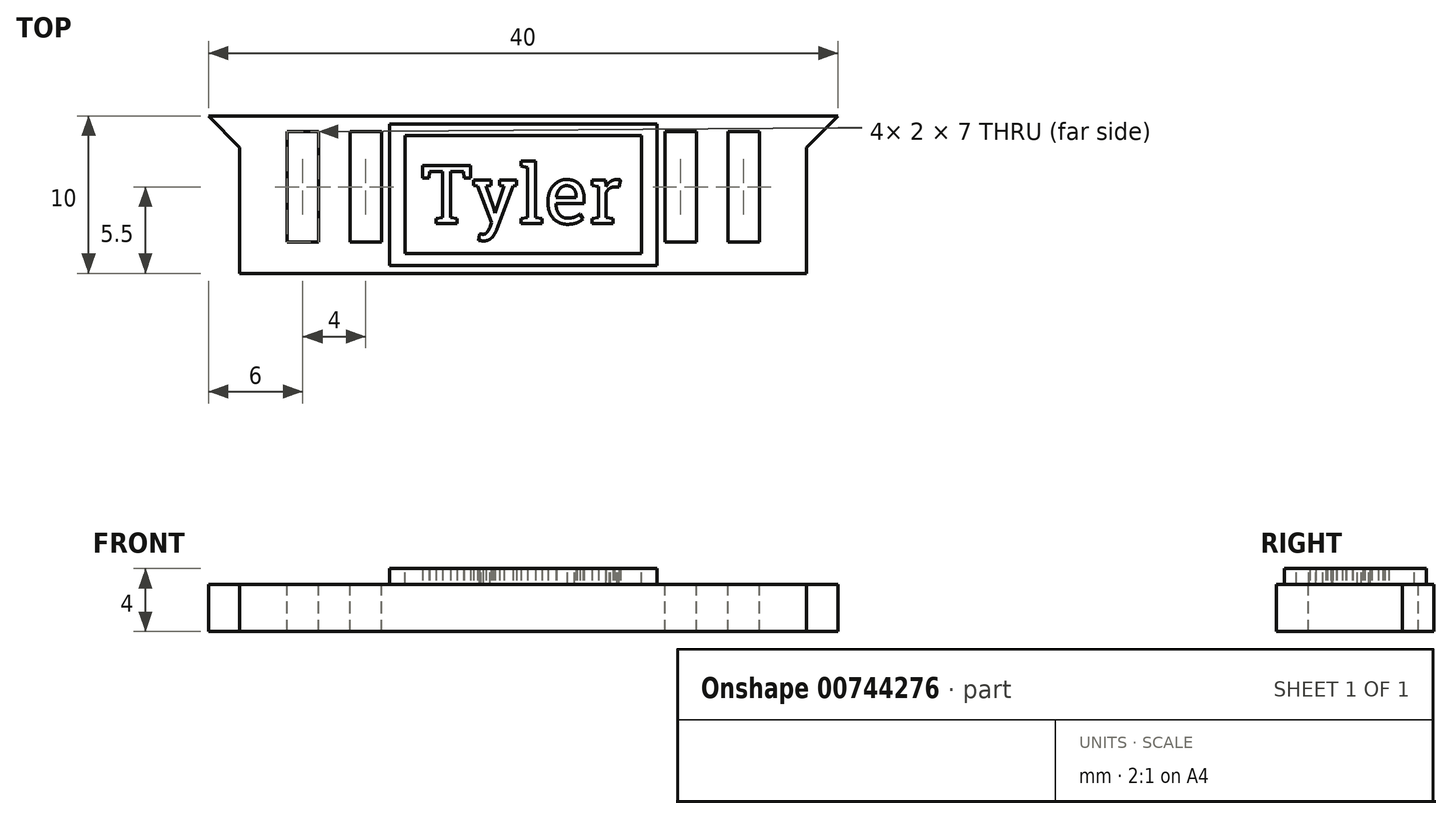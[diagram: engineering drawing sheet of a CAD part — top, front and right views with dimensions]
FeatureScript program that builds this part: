
annotation { "Feature Type Name" : "Feature", "Feature Type Description" : "" }
export const myFeature = defineFeature(function(context is Context, id is Id, definition is map)
    precondition{}
    {
        {
            var Q0;
            Q0=qCreatedBy(makeId("Top.planeOp"),FACE);
            var sketch = newSketch(context, id + "F0", { "sketchPlane" : qUnion([Q0])});
            skLineSegment(sketch, "E0.bottom", {"start": v(-18, 5) * mm, "end": v(18, 5) * mm});
            skLineSegment(sketch, "E0.top", {"start": v(-18, -5) * mm, "end": v(18, -5) * mm});
            skLineSegment(sketch, "E0.left", {"start": v(-18, 3) * mm, "end": v(-18, -5) * mm});
            skLineSegment(sketch, "E0.right", {"start": v(18, 3) * mm, "end": v(18, -5) * mm});
            skPoint(sketch, "E0.middle", {"position": v(0, 0) * mm});
            skLineSegment(sketch, "E1", {"start": v(18, 5) * mm, "end": v(20, 5) * mm});
            skLineSegment(sketch, "E2", {"start": v(20, 5) * mm, "end": v(18, 3) * mm});
            skLineSegment(sketch, "E3.MirrorCS", {"start": v(-20, 5) * mm, "end": v(-18, 3) * mm});
            skLineSegment(sketch, "E4.MirrorCS", {"start": v(-18, 5) * mm, "end": v(-20, 5) * mm});
            skSolve(sketch);
        }
        {
            var Q0;
            Q0=makeQuery(id+"F0.imprint","IMPRINT",FACE,{"disambiguationData":[TD([[makeQuery(id+"F0.imprint","IMPRINT",EDGE,{"derivedFrom":sQuery(id+"F0.wireOp",EDGE,"E0.bottom")}),-1.0]])]});
            extrude(context, id + "F1", {"entities" : qUnion([Q0]), "depth" : 3 * mm, "offsetDistance" : 25 * mm});
        }
        {
            var Q0;
            Q0=makeQuery(id+"F1.opExtrude","CAP_FACE",FACE,{"disambiguationData":[OSD([sQuery(id+"F0.wireOp",EDGE,"E0.bottom"),sQuery(id+"F0.wireOp",EDGE,"E0.top"),sQuery(id+"F0.wireOp",EDGE,"E0.left"),sQuery(id+"F0.wireOp",EDGE,"E0.right"),sQuery(id+"F0.wireOp",EDGE,"E1"),sQuery(id+"F0.wireOp",EDGE,"E2"),sQuery(id+"F0.wireOp",EDGE,"E3.MirrorCS"),sQuery(id+"F0.wireOp",EDGE,"E4.MirrorCS")])],"isStart":false});
            var sketch = newSketch(context, id + "F2", { "sketchPlane" : qUnion([Q0])});
            skLineSegment(sketch, "E5.bottom", {"start": v(-13, 4) * mm, "end": v(-15, 4) * mm});
            skLineSegment(sketch, "E5.top", {"start": v(-13, -3) * mm, "end": v(-15, -3) * mm});
            skLineSegment(sketch, "E5.left", {"start": v(-13, 4) * mm, "end": v(-13, -3) * mm});
            skLineSegment(sketch, "E5.right", {"start": v(-15, 4) * mm, "end": v(-15, -3) * mm});
            skLineSegment(sketch, "E6.1.0.0", {"start": v(-9, 4) * mm, "end": v(-9, -3) * mm});
            skLineSegment(sketch, "E6.1.0.1", {"start": v(-9, 4) * mm, "end": v(-11, 4) * mm});
            skLineSegment(sketch, "E6.1.0.2", {"start": v(-11, 4) * mm, "end": v(-11, -3) * mm});
            skLineSegment(sketch, "E6.1.0.3", {"start": v(-9, -3) * mm, "end": v(-11, -3) * mm});
            skLineSegment(sketch, "E6.2.0.0", {"start": v(-5, 4) * mm, "end": v(-5, -3) * mm});
            skLineSegment(sketch, "E6.2.0.1", {"start": v(-5, 4) * mm, "end": v(-7, 4) * mm});
            skLineSegment(sketch, "E6.2.0.2", {"start": v(-7, 4) * mm, "end": v(-7, -3) * mm});
            skLineSegment(sketch, "E6.2.0.3", {"start": v(-5, -3) * mm, "end": v(-7, -3) * mm});
            skLineSegment(sketch, "E6.3.0.0", {"start": v(-1, 4) * mm, "end": v(-1, -3) * mm});
            skLineSegment(sketch, "E6.3.0.1", {"start": v(-1, 4) * mm, "end": v(-3, 4) * mm});
            skLineSegment(sketch, "E6.3.0.2", {"start": v(-3, 4) * mm, "end": v(-3, -3) * mm});
            skLineSegment(sketch, "E6.3.0.3", {"start": v(-1, -3) * mm, "end": v(-3, -3) * mm});
            skLineSegment(sketch, "E6.4.0.0", {"start": v(3, 4) * mm, "end": v(3, -3) * mm});
            skLineSegment(sketch, "E6.4.0.1", {"start": v(3, 4) * mm, "end": v(1, 4) * mm});
            skLineSegment(sketch, "E6.4.0.2", {"start": v(1, 4) * mm, "end": v(1, -3) * mm});
            skLineSegment(sketch, "E6.4.0.3", {"start": v(3, -3) * mm, "end": v(1, -3) * mm});
            skLineSegment(sketch, "E6.5.0.0", {"start": v(7, 4) * mm, "end": v(7, -3) * mm});
            skLineSegment(sketch, "E6.5.0.1", {"start": v(7, 4) * mm, "end": v(5, 4) * mm});
            skLineSegment(sketch, "E6.5.0.2", {"start": v(5, 4) * mm, "end": v(5, -3) * mm});
            skLineSegment(sketch, "E6.5.0.3", {"start": v(7, -3) * mm, "end": v(5, -3) * mm});
            skLineSegment(sketch, "E6.6.0.0", {"start": v(11, 4) * mm, "end": v(11, -3) * mm});
            skLineSegment(sketch, "E6.6.0.1", {"start": v(11, 4) * mm, "end": v(9, 4) * mm});
            skLineSegment(sketch, "E6.6.0.2", {"start": v(9, 4) * mm, "end": v(9, -3) * mm});
            skLineSegment(sketch, "E6.6.0.3", {"start": v(11, -3) * mm, "end": v(9, -3) * mm});
            skLineSegment(sketch, "E6.7.0.0", {"start": v(15, 4) * mm, "end": v(15, -3) * mm});
            skLineSegment(sketch, "E6.7.0.1", {"start": v(15, 4) * mm, "end": v(13, 4) * mm});
            skLineSegment(sketch, "E6.7.0.2", {"start": v(13, 4) * mm, "end": v(13, -3) * mm});
            skLineSegment(sketch, "E6.7.0.3", {"start": v(15, -3) * mm, "end": v(13, -3) * mm});
            skLineSegment(sketch, "E6.direction1", {"start": v(-13, -3) * mm, "end": v(-9, -3) * mm, "construction": true});
            skSolve(sketch);
        }
        {
            var Q0;
            Q0 = qSketchRegion(id + "F2", true);
            extrude(context, id + "F3", {"entities" : qUnion([Q0]), "operationType" : NewBodyOperationType.REMOVE, "oppositeDirection" : true, "depth" : 25 * mm, "offsetDistance" : 25 * mm});
        }
        {
            var Q0;
            Q0=qCreatedBy(makeId("Top.planeOp"),FACE);
            var sketch = newSketch(context, id + "F4", { "sketchPlane" : qUnion([Q0])});
            skLineSegment(sketch, "E7.bottom", {"start": v(-8.5, 4.5) * mm, "end": v(8.5, 4.5) * mm});
            skLineSegment(sketch, "E7.top", {"start": v(-8.5, -4.5) * mm, "end": v(8.5, -4.5) * mm});
            skLineSegment(sketch, "E7.left", {"start": v(-8.5, 4.5) * mm, "end": v(-8.5, -4.5) * mm});
            skLineSegment(sketch, "E7.right", {"start": v(8.5, 4.5) * mm, "end": v(8.5, -4.5) * mm});
            skPoint(sketch, "E7.middle", {"position": v(0, 0) * mm});
            skSolve(sketch);
        }
        {
            var Q0;
            Q0 = qSketchRegion(id + "F4", true);
            extrude(context, id + "F5", {"entities" : qUnion([Q0]), "operationType" : NewBodyOperationType.ADD, "depth" : 4 * mm, "offsetDistance" : 25 * mm});
        }
        {
            var Q0;
            Q0=makeQuery(id+"F5.opExtrude","CAP_FACE",FACE,{"disambiguationData":[OSD([sQuery(id+"F4.wireOp",EDGE,"E7.bottom"),sQuery(id+"F4.wireOp",EDGE,"E7.top"),sQuery(id+"F4.wireOp",EDGE,"E7.left"),sQuery(id+"F4.wireOp",EDGE,"E7.right")])],"isStart":false});
            var sketch = newSketch(context, id + "F6", { "sketchPlane" : qUnion([Q0])});
            skLineSegment(sketch, "E8.bottom", {"start": v(-7.5, 3.75) * mm, "end": v(7.5, 3.75) * mm});
            skLineSegment(sketch, "E8.top", {"start": v(-7.5, -3.75) * mm, "end": v(7.5, -3.75) * mm});
            skLineSegment(sketch, "E8.left", {"start": v(-7.5, 3.75) * mm, "end": v(-7.5, -3.75) * mm});
            skLineSegment(sketch, "E8.right", {"start": v(7.5, 3.75) * mm, "end": v(7.5, -3.75) * mm});
            skPoint(sketch, "E8.middle", {"position": v(0, 0) * mm});
            skSolve(sketch);
        }
        {
            var Q0;
            Q0 = qSketchRegion(id + "F6", true);
            extrude(context, id + "F7", {"entities" : qUnion([Q0]), "operationType" : NewBodyOperationType.REMOVE, "oppositeDirection" : true, "depth" : 1 * mm, "offsetDistance" : 25 * mm});
        }
        {
            var Q0;
            Q0=makeQuery(id+"F7.boolean.opBoolean","COPY",FACE,{"derivedFrom":makeQuery(id+"F7.opExtrude","CAP_FACE",FACE,{"disambiguationData":[OSD([sQuery(id+"F6.wireOp",EDGE,"E8.bottom"),sQuery(id+"F6.wireOp",EDGE,"E8.top"),sQuery(id+"F6.wireOp",EDGE,"E8.left"),sQuery(id+"F6.wireOp",EDGE,"E8.right")])],"isStart":false})});
            var sketch = newSketch(context, id + "F8", { "sketchPlane" : qUnion([Q0])});
            skText(sketch, "E9", { "text": "Tyler", "fontName": "RobotoSlab-Regular.ttf"});
            const initialGuessF8  = {"E9": [-0.0065, -0.00183, 1, 0, 0.00374]};
            skSetInitialGuess(sketch, initialGuessF8);
            skSolve(sketch);
        }
        {
            var Q0;
            Q0 = qSketchRegion(id + "F8", true);
            extrude(context, id + "F9", {"entities" : qUnion([Q0]), "operationType" : NewBodyOperationType.ADD, "depth" : 1 * mm, "offsetDistance" : 25 * mm});
        }
    });
